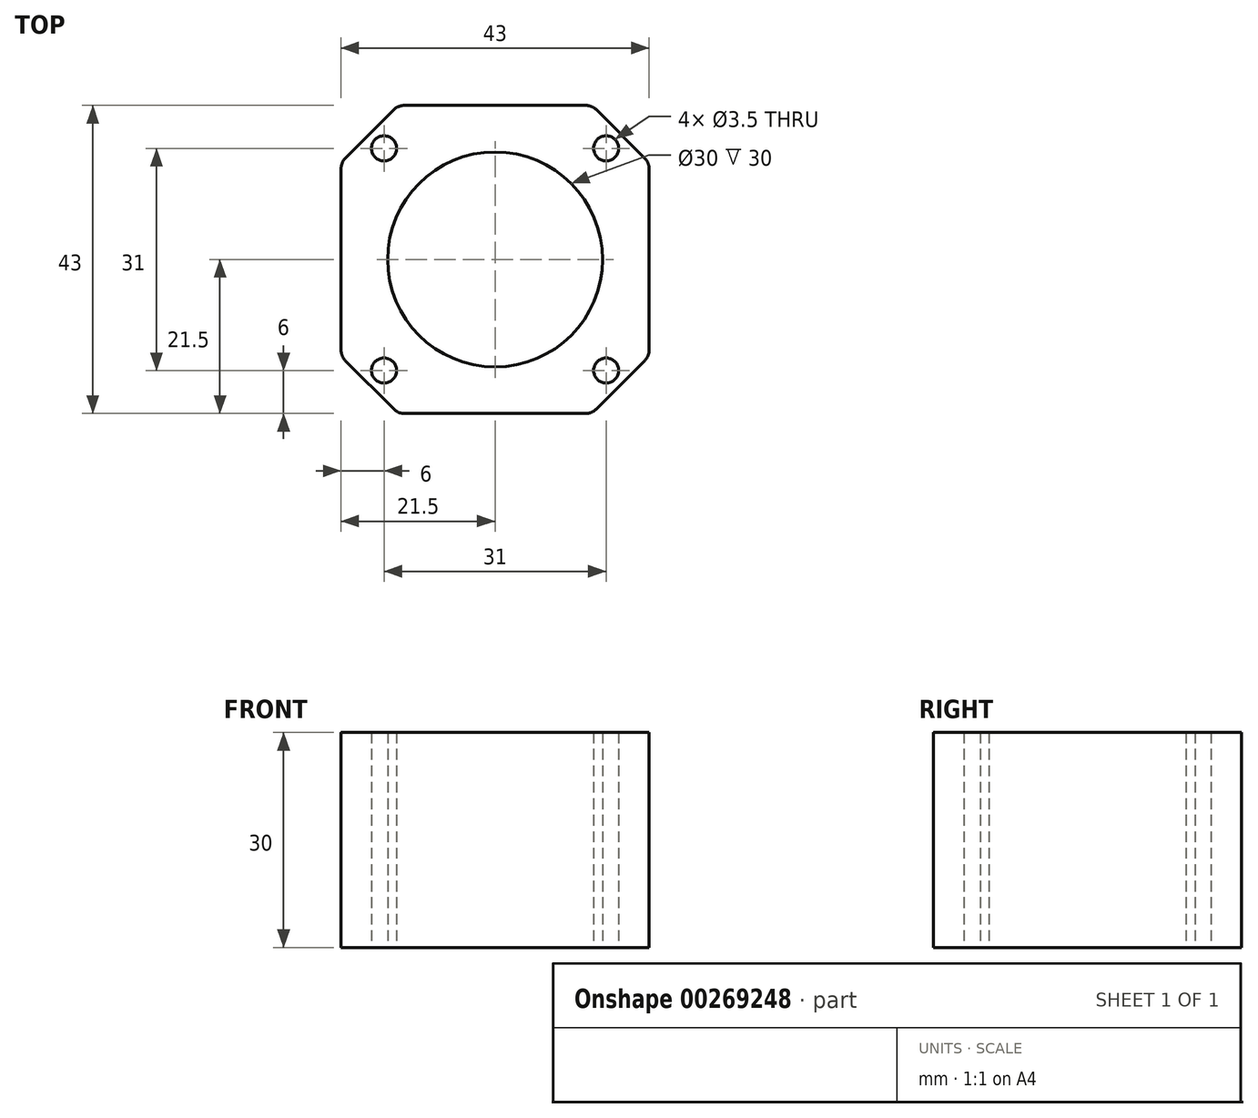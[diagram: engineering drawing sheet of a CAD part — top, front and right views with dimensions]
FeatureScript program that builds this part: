
annotation { "Feature Type Name" : "Feature", "Feature Type Description" : "" }
export const myFeature = defineFeature(function(context is Context, id is Id, definition is map)
    precondition{}
    {
        {
            var Q0;
            Q0=qCreatedBy(makeId("Top.planeOp"),FACE);
            var sketch = newSketch(context, id + "F0", { "sketchPlane" : qUnion([Q0])});
            skLineSegment(sketch, "E0.bottom", {"start": v(-21.5, 21.5) * mm, "end": v(21.5, 21.5) * mm});
            skLineSegment(sketch, "E0.top", {"start": v(-21.5, -21.5) * mm, "end": v(21.5, -21.5) * mm});
            skLineSegment(sketch, "E0.left", {"start": v(-21.5, 21.5) * mm, "end": v(-21.5, -21.5) * mm});
            skLineSegment(sketch, "E0.right", {"start": v(21.5, 21.5) * mm, "end": v(21.5, -21.5) * mm});
            skPoint(sketch, "E1", {"position": v(0, 21.5) * mm});
            skPoint(sketch, "E2", {"position": v(-21.5, 0) * mm});
            skCircle(sketch, "E3", {"center": v(0, 0) * mm, "radius": 15 * mm});
            skLineSegment(sketch, "E4.bottom", {"start": v(-15.5, 15.5) * mm, "end": v(15.5, 15.5) * mm, "construction": true});
            skLineSegment(sketch, "E4.top", {"start": v(-15.5, -15.5) * mm, "end": v(15.5, -15.5) * mm, "construction": true});
            skLineSegment(sketch, "E4.left", {"start": v(-15.5, 15.5) * mm, "end": v(-15.5, -15.5) * mm, "construction": true});
            skLineSegment(sketch, "E4.right", {"start": v(15.5, 15.5) * mm, "end": v(15.5, -15.5) * mm, "construction": true});
            skPoint(sketch, "E5", {"position": v(15.5, 0) * mm});
            skPoint(sketch, "E6", {"position": v(0, -15.5) * mm});
            skCircle(sketch, "E7", {"center": v(-15.5, 15.5) * mm, "radius": 1.75 * mm});
            skCircle(sketch, "E8", {"center": v(15.5, 15.5) * mm, "radius": 1.75 * mm});
            skCircle(sketch, "E9", {"center": v(15.5, -15.5) * mm, "radius": 1.75 * mm});
            skCircle(sketch, "E10", {"center": v(-15.5, -15.5) * mm, "radius": 1.75 * mm});
            skSolve(sketch);
        }
        {
            var Q0;
            Q0=makeQuery(id+"F0.imprint","IMPRINT",FACE,{"disambiguationData":[TD([[makeQuery(id+"F0.imprint","IMPRINT",EDGE,{"derivedFrom":sQuery(id+"F0.wireOp",EDGE,"E0.bottom")}),-1.0]])]});
            extrude(context, id + "F1", {"entities" : qUnion([Q0]), "depth" : 30 * mm});
        }
        {
            var Q0;
            Q0=makeQuery(id+"F1.opExtrude","SWEPT_EDGE",EDGE,{"disambiguationData":[OSD([sQuery(id+"F0.wireOp",EDGE,"E0.top"),sQuery(id+"F0.wireOp",EDGE,"E0.left")])]});
            var Q1;
            Q1=makeQuery(id+"F1.opExtrude","SWEPT_EDGE",EDGE,{"disambiguationData":[OSD([sQuery(id+"F0.wireOp",EDGE,"E0.top"),sQuery(id+"F0.wireOp",EDGE,"E0.right")])]});
            var Q2;
            Q2=makeQuery(id+"F1.opExtrude","SWEPT_EDGE",EDGE,{"disambiguationData":[OSD([sQuery(id+"F0.wireOp",EDGE,"E0.bottom"),sQuery(id+"F0.wireOp",EDGE,"E0.right")])]});
            var Q3;
            Q3=makeQuery(id+"F1.opExtrude","SWEPT_EDGE",EDGE,{"disambiguationData":[OSD([sQuery(id+"F0.wireOp",EDGE,"E0.bottom"),sQuery(id+"F0.wireOp",EDGE,"E0.left")])]});
            chamfer(context, id + "F2", {"entities" : qUnion([Q0, Q1, Q2, Q3]), "width" : 8 * mm, "tangentPropagation" : true});
        }
        {
            var Q0;
            {var subQ0=sQuery(id+"F0.wireOp",EDGE,"E0.bottom");Q0=makeQuery(id+"F2.opChamfer","BLEND_EDGE",EDGE,{"blendedFrom":[makeQuery(id+"F1.opExtrude","SWEPT_EDGE",EDGE,{"disambiguationData":[OSD([subQ0,sQuery(id+"F0.wireOp",EDGE,"E0.left")])]}),makeQuery(id+"F1.opExtrude","SWEPT_FACE",FACE,{"disambiguationData":[OSD([subQ0])]})],"blendedInto":[makeQuery(id+"F1.opExtrude","SWEPT_FACE",FACE,{"disambiguationData":[OSD([subQ0])]})]});}
            var Q1;
            {var subQ0=sQuery(id+"F0.wireOp",EDGE,"E0.bottom");Q1=makeQuery(id+"F2.opChamfer","BLEND_EDGE",EDGE,{"blendedFrom":[makeQuery(id+"F1.opExtrude","SWEPT_EDGE",EDGE,{"disambiguationData":[OSD([subQ0,sQuery(id+"F0.wireOp",EDGE,"E0.right")])]}),makeQuery(id+"F1.opExtrude","SWEPT_FACE",FACE,{"disambiguationData":[OSD([subQ0])]})],"blendedInto":[makeQuery(id+"F1.opExtrude","SWEPT_FACE",FACE,{"disambiguationData":[OSD([subQ0])]})]});}
            var Q2;
            {var subQ0=sQuery(id+"F0.wireOp",EDGE,"E0.right");Q2=makeQuery(id+"F2.opChamfer","BLEND_EDGE",EDGE,{"blendedFrom":[makeQuery(id+"F1.opExtrude","SWEPT_EDGE",EDGE,{"disambiguationData":[OSD([sQuery(id+"F0.wireOp",EDGE,"E0.bottom"),subQ0])]}),makeQuery(id+"F1.opExtrude","SWEPT_FACE",FACE,{"disambiguationData":[OSD([subQ0])]})],"blendedInto":[makeQuery(id+"F1.opExtrude","SWEPT_FACE",FACE,{"disambiguationData":[OSD([subQ0])]})]});}
            var Q3;
            {var subQ0=sQuery(id+"F0.wireOp",EDGE,"E0.left");Q3=makeQuery(id+"F2.opChamfer","BLEND_EDGE",EDGE,{"blendedFrom":[makeQuery(id+"F1.opExtrude","SWEPT_EDGE",EDGE,{"disambiguationData":[OSD([sQuery(id+"F0.wireOp",EDGE,"E0.bottom"),subQ0])]}),makeQuery(id+"F1.opExtrude","SWEPT_FACE",FACE,{"disambiguationData":[OSD([subQ0])]})],"blendedInto":[makeQuery(id+"F1.opExtrude","SWEPT_FACE",FACE,{"disambiguationData":[OSD([subQ0])]})]});}
            var Q4;
            {var subQ0=sQuery(id+"F0.wireOp",EDGE,"E0.right");Q4=makeQuery(id+"F2.opChamfer","BLEND_EDGE",EDGE,{"blendedFrom":[makeQuery(id+"F1.opExtrude","SWEPT_EDGE",EDGE,{"disambiguationData":[OSD([sQuery(id+"F0.wireOp",EDGE,"E0.top"),subQ0])]}),makeQuery(id+"F1.opExtrude","SWEPT_FACE",FACE,{"disambiguationData":[OSD([subQ0])]})],"blendedInto":[makeQuery(id+"F1.opExtrude","SWEPT_FACE",FACE,{"disambiguationData":[OSD([subQ0])]})]});}
            var Q5;
            {var subQ0=sQuery(id+"F0.wireOp",EDGE,"E0.top");Q5=makeQuery(id+"F2.opChamfer","BLEND_EDGE",EDGE,{"blendedFrom":[makeQuery(id+"F1.opExtrude","SWEPT_EDGE",EDGE,{"disambiguationData":[OSD([subQ0,sQuery(id+"F0.wireOp",EDGE,"E0.right")])]}),makeQuery(id+"F1.opExtrude","SWEPT_FACE",FACE,{"disambiguationData":[OSD([subQ0])]})],"blendedInto":[makeQuery(id+"F1.opExtrude","SWEPT_FACE",FACE,{"disambiguationData":[OSD([subQ0])]})]});}
            var Q6;
            {var subQ0=sQuery(id+"F0.wireOp",EDGE,"E0.top");Q6=makeQuery(id+"F2.opChamfer","BLEND_EDGE",EDGE,{"blendedFrom":[makeQuery(id+"F1.opExtrude","SWEPT_EDGE",EDGE,{"disambiguationData":[OSD([subQ0,sQuery(id+"F0.wireOp",EDGE,"E0.left")])]}),makeQuery(id+"F1.opExtrude","SWEPT_FACE",FACE,{"disambiguationData":[OSD([subQ0])]})],"blendedInto":[makeQuery(id+"F1.opExtrude","SWEPT_FACE",FACE,{"disambiguationData":[OSD([subQ0])]})]});}
            var Q7;
            {var subQ0=sQuery(id+"F0.wireOp",EDGE,"E0.left");Q7=makeQuery(id+"F2.opChamfer","BLEND_EDGE",EDGE,{"blendedFrom":[makeQuery(id+"F1.opExtrude","SWEPT_EDGE",EDGE,{"disambiguationData":[OSD([sQuery(id+"F0.wireOp",EDGE,"E0.top"),subQ0])]}),makeQuery(id+"F1.opExtrude","SWEPT_FACE",FACE,{"disambiguationData":[OSD([subQ0])]})],"blendedInto":[makeQuery(id+"F1.opExtrude","SWEPT_FACE",FACE,{"disambiguationData":[OSD([subQ0])]})]});}
            fillet(context, id + "F3", {"entities" : qUnion([Q0, Q1, Q2, Q3, Q4, Q5, Q6, Q7]), "radius" : 2 * mm, "tangentPropagation" : true, "allowEdgeOverflow" : false});
        }
    });
